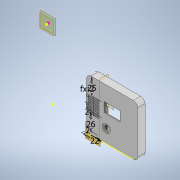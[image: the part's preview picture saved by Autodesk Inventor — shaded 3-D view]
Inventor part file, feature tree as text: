
AUTODESK INVENTOR PART (.ipt)
format: ipt  version: 2022.2 (Build 262287010, 287A)  size: 606,720 bytes
history: native  units: mm
features: sketch x20, extrude x18, plane x8, chamfer x1, projected_geometry x1
ambient origin geometry x8: Origin, YZ Plane, XZ Plane, XY Plane, X Axis, Y Axis, Z Axis, Center Point
bodies: Volumenkörper1 (feature_tree)
feature tree (48):
  plane  "Arbeitsebene1"
  extrude  "Extrusion1"  Depth=2.0mm
  extrude  "Extrusion2"  Depth=24.0mm
  extrude  "Extrusion3"  Depth=71.8mm
  sketch  "Skizze4"  dims[d9=23.9mm d10=21.0mm]
  plane  "Arbeitsebene10"
  sketch  "Skizze5"  dims[d13=2.0mm d14=0.0mm d15=2.0mm]
  sketch  "Skizze6"  dims[d16=9.0mm d17=0.0mm d18=1.6mm]
  plane  "Arbeitsebene2"
  plane  "Arbeitsebene4"
  extrude  "Extrusion9"  Depth=21.0mm
  extrude  "Extrusion10"  Depth=2.0mm
  plane  "Arbeitsebene5"
  extrude  "Extrusion11"  Depth=1.6mm
  plane  "Arbeitsebene8"
  extrude  "Extrusion12"  Depth=7.3mm
  extrude  "Extrusion13"  Depth=25.0mm
  extrude  "Extrusion8"  Depth=2.0mm
  extrude  "Extrusion14"  Depth=2.0mm
  plane  "Arbeitsebene9"
  extrude  "Extrusion15"  Depth=16.0mm
  extrude  "Extrusion16"  Depth=2.0mm TaperAngle=0.0deg
  sketch  "Skizze18"  dims[d51=1.2mm d52=70.0mm d54=2.4mm d55=10.0mm d57=10.0mm]
  extrude  "Extrusion17"  Depth=1.2mm
  extrude  "Extrusion18"  Depth=2.4mm
  extrude  "Extrusion19"  Depth=1.2mm
  plane  "Arbeitsebene7"
  sketch  "Skizze21"  dims[d71=2.0mm d74=2.9mm d75=0.0mm]
  extrude  "Extrusion20"  Depth=1.4mm TaperAngle=0.0deg
  extrude  "Extrusion21"  Depth=2.0mm TaperAngle=0.0deg
  chamfer  "Fase1"  Distance=8.0mm
  extrude  "Extrusion22"  Depth=27.0mm
  sketch  "Skizze1"  dims[d0=9.0mm d2=2.0mm]
  sketch  "Skizze2"  dims[d3=7.5mm d6=24.0mm]
  sketch  "Skizze3"  dims[d7=14.0mm d8=71.8mm]
  projected_geometry  "Projizierte Kontur1"
  sketch  "Skizze9"  dims[d19=18.3mm d20=7.3mm]
  sketch  "Skizze11"  dims[d21=51.75mm d22=22.0mm d23=0.0mm d24=0.0mm d25=25.0mm]
  sketch  "Skizze13"  dims[d26=26.0mm d29=2.0mm]
  sketch  "Skizze14"  dims[d30=2.0mm d33=2.0mm]
  sketch  "Skizze15"  dims[d41=10.0mm d42=0.0mm d43=16.0mm]
  sketch  "Skizze16"  dims[d44=23.0mm d46=2.0mm d47=0.0mm]
  sketch  "Skizze17"  dims[d48=10.0mm d49=0.0mm d50=1.2mm]
  sketch  "Skizze19"  dims[d59=1.4mm d60=0.0mm d61=1.2mm]
  sketch  "Skizze20"  dims[d62=70.0mm d64=3.0mm d65=10.0mm d67=10.0mm d69=1.4mm d70=0.0mm]
  sketch  "Skizze22"  dims[d76=2.0mm]
  sketch  "Skizze23"  dims[d77=27.0mm]
  sketch  "Skizze24"  dims[d78=0.0mm d79=8.0mm d80=27.0mm d81=3.5mm d82=0.0mm d83=3.5mm d84=0.0mm d85=2.0mm d86=3.5mm d87=0.0mm d88=12.0mm d89=2.5mm d90=4.0mm d91=7.6mm d92=1.4mm d93=0.0mm d94=1.0mm d95=0.0mm d96=3.0mm d97=3.0mm d98=1.0mm d99=0.0mm d100=3.0mm d101=3.0mm d102=22.0mm d103=2.0mm d104=1.0mm d105=1.0mm d106=1.0mm d107=51.75mm d108=0.0mm d109=1.0mm d110=3.0mm d111=21.5mm d112=2.5mm d113=0.0mm d114=2.5mm d115=1.0mm d116=8.0mm d117=1.5mm d118=2.0mm d119=45.0deg d120=31.699999mm d121=61.6mm d122=71.799999mm d123=6.4mm d124=6.4mm d125=6.4mm d126=6.4mm d127=17.911999mm d128=16.804mm d129=10.206mm d130=10.206mm d131=27.198mm d132=17.829999mm d133=8.7mm d134=8.7mm d135=1.0mm d136=0.0mm]
